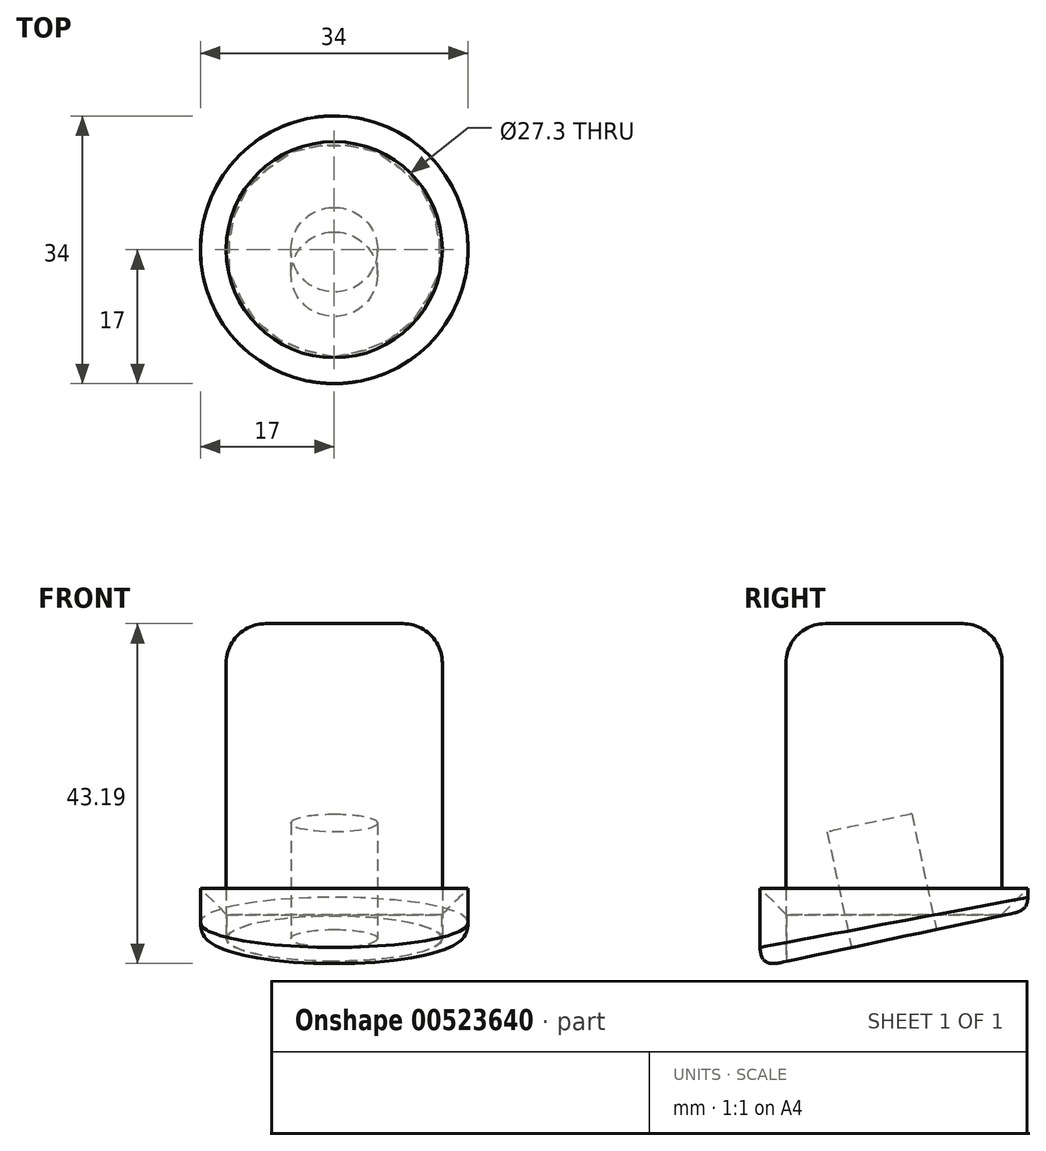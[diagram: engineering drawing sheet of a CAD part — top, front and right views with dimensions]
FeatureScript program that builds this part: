
annotation { "Feature Type Name" : "Feature", "Feature Type Description" : "" }
export const myFeature = defineFeature(function(context is Context, id is Id, definition is map)
    precondition{}
    {
        {
            var Q0;
            Q0=qCreatedBy(makeId("Top.planeOp"),FACE);
            var sketch = newSketch(context, id + "F0", { "sketchPlane" : qUnion([Q0])});
            skLineSegment(sketch, "E0", {"start": v(-30.36, 0) * mm, "end": v(39.37, 0) * mm});
            skSolve(sketch);
        }
        {
            var Q0;
            Q0=qCreatedBy(makeId("Top.planeOp"),FACE);
            var Q1;
            Q1=sQuery(id+"F0.wireOp",EDGE,"E0");
            cPlane(context, id + "F1", {"entities" : qUnion([Q0, Q1]), "cplaneType" : CPlaneType.LINE_ANGLE, "offset" : 25 * mm, "angle" : 12 * degree, "width" : 150 * mm, "height" : 150 * mm});
        }
        {
            var Q0;
            Q0=qCreatedBy(makeId("Top.planeOp"),FACE);
            var sketch = newSketch(context, id + "F2", { "sketchPlane" : qUnion([Q0])});
            skCircle(sketch, "E1", {"center": v(0, 0) * mm, "radius": 13.73 * mm});
            skSolve(sketch);
        }
        {
            var Q0;
            Q0 = qSketchRegion(id + "F2", true);
            var Q1;
            Q1 = qBodyType(qCreatedBy(id + "F1" ,FACE), BodyType.SOLID);
            extrude(context, id + "F3", {"entities" : qUnion([Q0]), "endBound" : BoundingType.SYMMETRIC, "depth" : 80 * mm, "endBoundEntityFace" : qUnion([Q1]), "offsetDistance" : 25 * mm});
        }
        {
            var Q0;
            Q0=makeQuery(id+"F3.opExtrude","CAP_EDGE",EDGE,{"disambiguationData":[OSD([sQuery(id+"F2.wireOp",EDGE,"E1")])],"isStart":false});
            fillet(context, id + "F4", {"entities" : qUnion([Q0]), "radius" : 5 * mm, "tangentPropagation" : true, "allowEdgeOverflow" : false});
        }
        {
            var Q0;
            Q0=qCreatedBy(id+"F1.planeOp",FACE);
            var sketch = newSketch(context, id + "F5", { "sketchPlane" : qUnion([Q0])});
            skCircle(sketch, "E2", {"center": v(0, 0) * mm, "radius": 5.5 * mm});
            skSolve(sketch);
        }
        {
            var Q0;
            Q0 = qSketchRegion(id + "F5", true);
            extrude(context, id + "F6", {"entities" : qUnion([Q0]), "endBound" : BoundingType.SYMMETRIC, "oppositeDirection" : true, "depth" : 30 * mm, "offsetDistance" : 25 * mm});
        }
        {
            var Q0;
            Q0=qCreatedBy(makeId("Top.planeOp"),FACE);
            var sketch = newSketch(context, id + "F7", { "sketchPlane" : qUnion([Q0])});
            skCircle(sketch, "E3", {"center": v(0, 0) * mm, "radius": 13.65 * mm});
            skCircle(sketch, "E4", {"center": v(0, 0) * mm, "radius": 17 * mm});
            skLineSegment(sketch, "E5", {"start": v(-28.46, 0) * mm, "end": v(40.56, 0) * mm});
            skSolve(sketch);
        }
        {
            var Q0;
            Q0 = qSketchRegion(id + "F7", true);
            extrude(context, id + "F8", {"entities" : qUnion([Q0]), "endBound" : BoundingType.SYMMETRIC, "depth" : 16 * mm, "offsetDistance" : 25 * mm});
        }
        {
            var Q0;
            Q0=makeQuery(id+"F8.opExtrude","CAP_EDGE",EDGE,{"disambiguationData":[OSD([sQuery(id+"F7.wireOp",EDGE,"E3")])],"isStart":false});
            chamfer(context, id + "F9", {"entities" : qUnion([Q0]), "width" : 5 * mm, "tangentPropagation" : true});
        }
        {
            var Q0;
            Q0=makeQuery(id+"F6.opExtrude","SWEPT_BODY",BODY,{"disambiguationData":[OSD([sQuery(id+"F5.wireOp",EDGE,"E2")])]});
            var Q1;
            Q1=makeQuery(id+"FhAeBmZyEPKih8r_2.opExtrude","SWEPT_BODY",BODY,{"disambiguationData":[OSD([sQuery(id+"FaX2KsitYL3Uy2I_2.wireOp",EDGE,"D38vE5yf-wFTs-OQtz-xDrl-5Hj7RrmYkQL9")])]});
            var Q2;
            Q2=makeQuery(id+"F3.opExtrude","SWEPT_BODY",BODY,{"disambiguationData":[OSD([sQuery(id+"F2.wireOp",EDGE,"E1")])]});
            booleanBodies(context, id + "F10", {"operationType" : BooleanOperationType.SUBTRACTION, "tools" : qUnion([Q0, Q1]), "targets" : qUnion([Q2])});
        }
        {
            var Q0;
            Q0=qCreatedBy(id+"F1.planeOp",FACE);
            var sketch = newSketch(context, id + "F11", { "sketchPlane" : qUnion([Q0])});
            skCircle(sketch, "E6", {"center": v(0, 0) * mm, "radius": 22.5 * mm});
            skSolve(sketch);
        }
        {
            var Q0;
            Q0 = qSketchRegion(id + "F11", true);
            extrude(context, id + "F12", {"entities" : qUnion([Q0]), "depth" : 55 * mm, "offsetDistance" : 25 * mm});
        }
        {
            var Q0;
            Q0=makeQuery(id+"F12.opExtrude","SWEPT_BODY",BODY,{"disambiguationData":[OSD([sQuery(id+"F11.wireOp",EDGE,"E6")])]});
            var Q1;
            Q1=makeQuery(id+"F3.opExtrude","SWEPT_BODY",BODY,{"disambiguationData":[OSD([sQuery(id+"F2.wireOp",EDGE,"E1")])]});
            var Q2;
            Q2=makeQuery(id+"F8.opExtrude","SWEPT_BODY",BODY,{"disambiguationData":[OSD([sQuery(id+"F7.wireOp",EDGE,"E3"),sQuery(id+"F7.wireOp",EDGE,"E4")])]});
            booleanBodies(context, id + "F13", {"operationType" : BooleanOperationType.SUBTRACTION, "tools" : qUnion([Q0]), "targets" : qUnion([Q1, Q2])});
        }
        {
            var Q0;
            Q0=makeQuery(id+"F13.opBoolean","INTERSECT",EDGE,{"derivedFrom":[makeQuery(id+"F8.opExtrude","SWEPT_FACE",FACE,{"disambiguationData":[OSD([sQuery(id+"F7.wireOp",EDGE,"E4")])]}),makeQuery(id+"F12.opExtrude","CAP_FACE",FACE,{"disambiguationData":[OSD([sQuery(id+"F11.wireOp",EDGE,"E6")])],"isStart":true})]});
            fillet(context, id + "F14", {"entities" : qUnion([Q0]), "radius" : 2 * mm, "tangentPropagation" : true, "rho" : 0.5, "crossSection" : FilletCrossSection.CONIC, "allowEdgeOverflow" : false});
        }
    });
